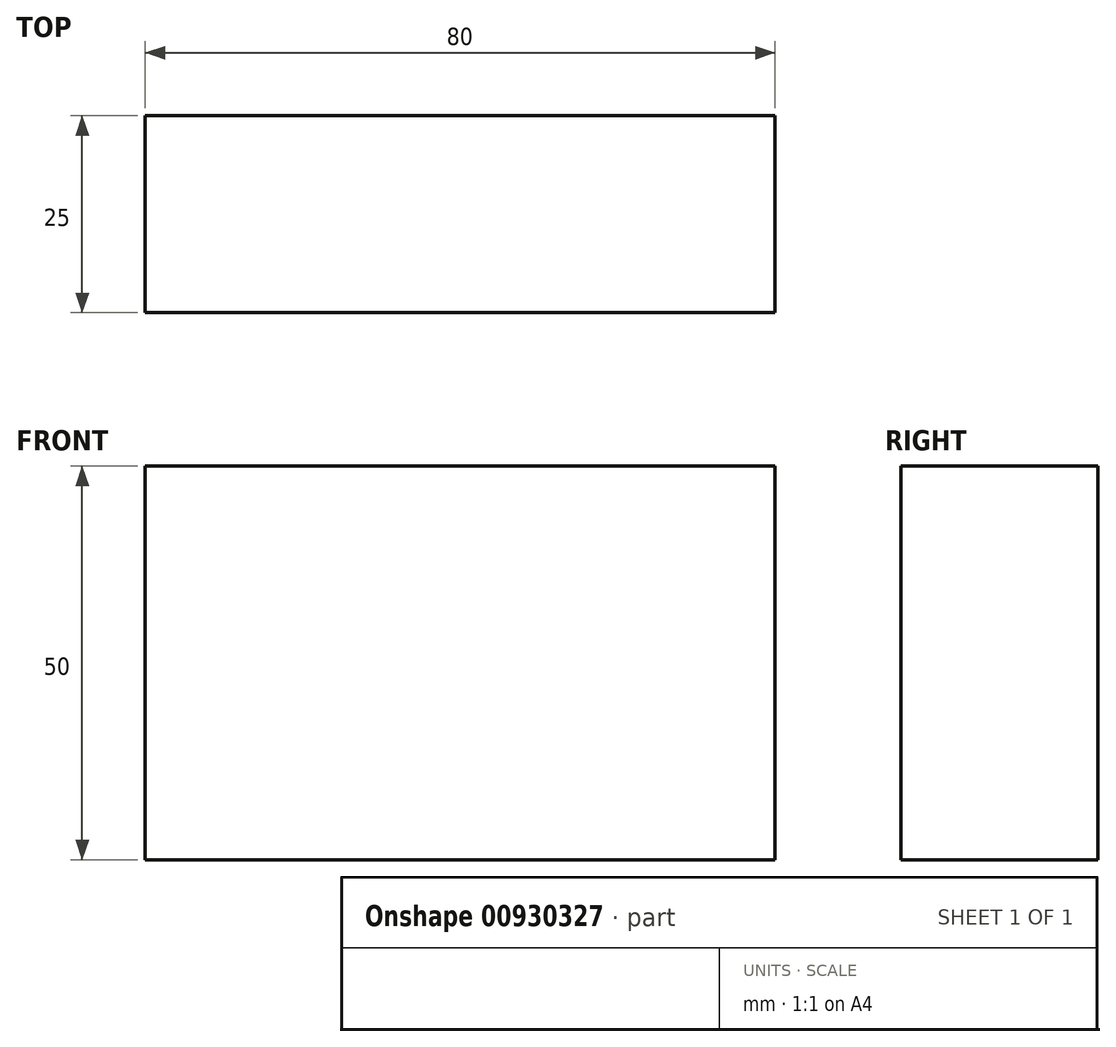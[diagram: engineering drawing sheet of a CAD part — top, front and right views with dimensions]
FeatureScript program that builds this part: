
annotation { "Feature Type Name" : "Feature", "Feature Type Description" : "" }
export const myFeature = defineFeature(function(context is Context, id is Id, definition is map)
    precondition{}
    {
        {
            var Q0;
            Q0=qCreatedBy(makeId("Front.planeOp"),FACE);
            var sketch = newSketch(context, id + "F0", { "sketchPlane" : qUnion([Q0])});
            skLineSegment(sketch, "E0.bottom", {"start": v(-40, -25) * mm, "end": v(40, -25) * mm});
            skLineSegment(sketch, "E0.top", {"start": v(-40, 25) * mm, "end": v(40, 25) * mm});
            skLineSegment(sketch, "E0.left", {"start": v(-40, -25) * mm, "end": v(-40, 25) * mm});
            skLineSegment(sketch, "E0.right", {"start": v(40, -25) * mm, "end": v(40, 25) * mm});
            skPoint(sketch, "E0.middle", {"position": v(0, 0) * mm});
            skSolve(sketch);
        }
        {
            var Q0;
            Q0 = qSketchRegion(id + "F0", true);
            extrude(context, id + "F1", {"entities" : qUnion([Q0]), "depth" : 25 * mm, "offsetDistance" : 25 * mm});
        }
    });
